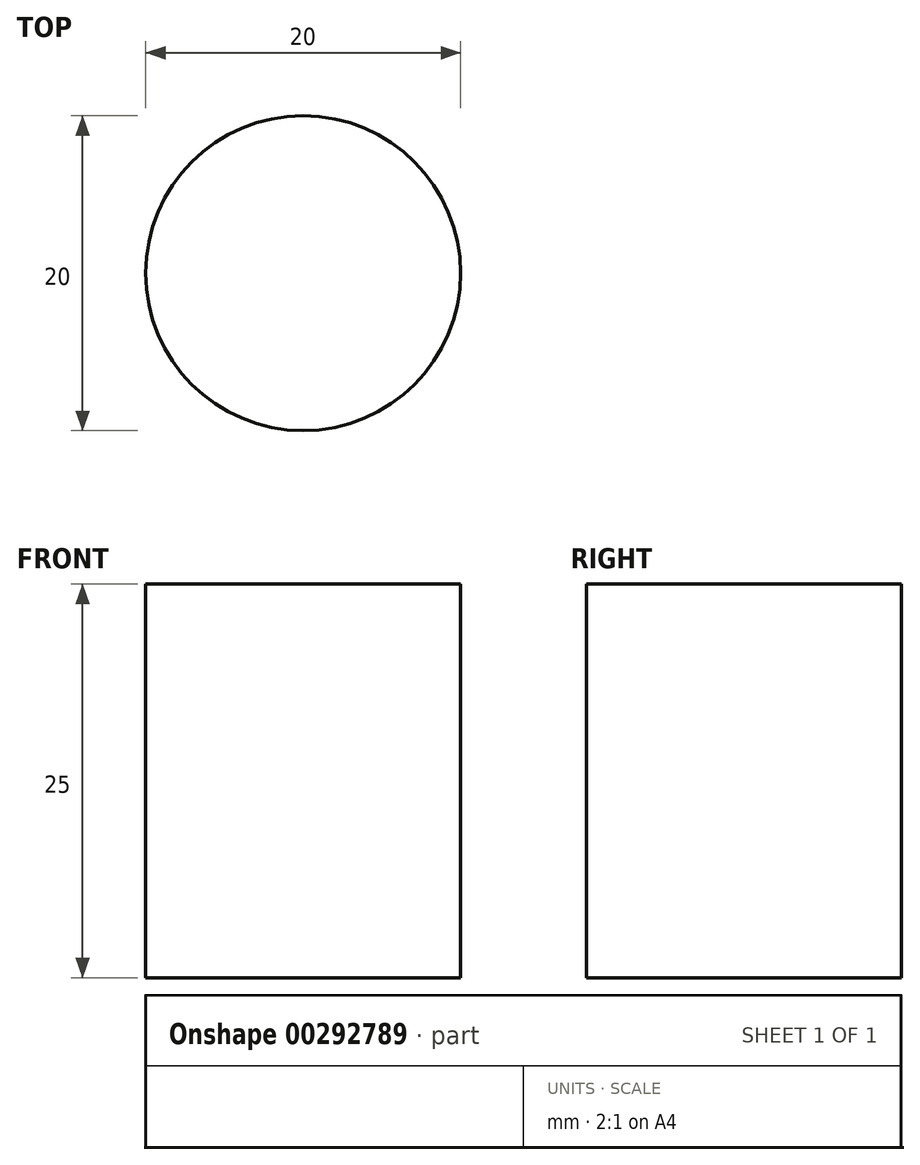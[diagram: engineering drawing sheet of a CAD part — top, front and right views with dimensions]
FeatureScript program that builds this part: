
annotation { "Feature Type Name" : "Feature", "Feature Type Description" : "" }
export const myFeature = defineFeature(function(context is Context, id is Id, definition is map)
    precondition{}
    {
        {
            var Q0;
            Q0=qCreatedBy(makeId("Top.planeOp"),FACE);
            var sketch = newSketch(context, id + "F0", { "sketchPlane" : qUnion([Q0])});
            skCircle(sketch, "E0", {"center": v(0, 0) * mm, "radius": 10 * mm});
            skSolve(sketch);
        }
        {
            var Q0;
            Q0 = qSketchRegion(id + "F0", true);
            extrude(context, id + "F1", {"entities" : qUnion([Q0]), "depth" : 25 * mm});
        }
        {
            var Q0;
            Q0=qCreatedBy(makeId("Front.planeOp"),FACE);
            cPlane(context, id + "F2", {"entities" : qUnion([Q0]), "cplaneType" : CPlaneType.OFFSET, "offset" : 10 * mm, "width" : 150 * mm, "height" : 150 * mm});
        }
    });
